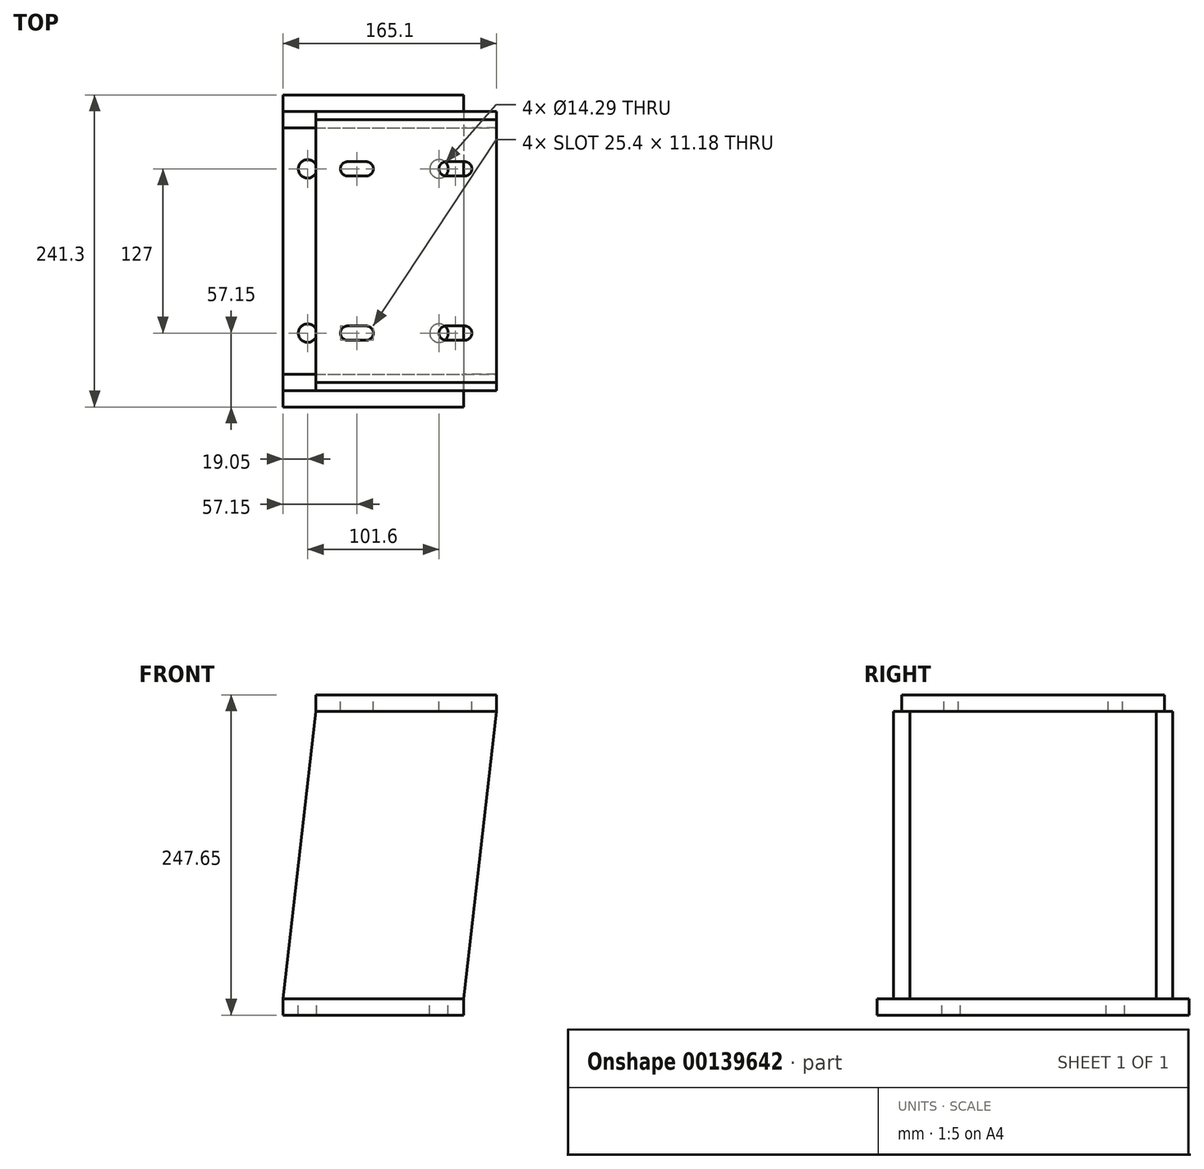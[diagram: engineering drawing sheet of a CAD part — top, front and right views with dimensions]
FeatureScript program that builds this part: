
annotation { "Feature Type Name" : "Feature", "Feature Type Description" : "" }
export const myFeature = defineFeature(function(context is Context, id is Id, definition is map)
    precondition{}
    {
        {
            var Q0;
            Q0=qCreatedBy(makeId("Top.planeOp"),FACE);
            var sketch = newSketch(context, id + "F0", { "sketchPlane" : qUnion([Q0])});
            skLineSegment(sketch, "E0.bottom", {"start": v(-69.85, 120.65) * mm, "end": v(69.85, 120.65) * mm});
            skLineSegment(sketch, "E0.top", {"start": v(-69.85, -120.65) * mm, "end": v(69.85, -120.65) * mm});
            skLineSegment(sketch, "E0.left", {"start": v(-69.85, 120.65) * mm, "end": v(-69.85, -120.65) * mm});
            skLineSegment(sketch, "E0.right", {"start": v(69.85, 120.65) * mm, "end": v(69.85, -120.65) * mm});
            skPoint(sketch, "E0.middle", {"position": v(0, 0) * mm});
            skSolve(sketch);
        }
        {
            var Q0;
            Q0 = qSketchRegion(id + "F0", true);
            extrude(context, id + "F1", {"entities" : qUnion([Q0]), "depth" : 12.7 * mm});
        }
        {
            var Q0;
            Q0=makeQuery(id+"F1.opExtrude","CAP_FACE",FACE,{"disambiguationData":[OSD([sQuery(id+"F0.wireOp",EDGE,"E0.bottom"),sQuery(id+"F0.wireOp",EDGE,"E0.top"),sQuery(id+"F0.wireOp",EDGE,"E0.left"),sQuery(id+"F0.wireOp",EDGE,"E0.right")])],"isStart":false});
            var sketch = newSketch(context, id + "F2", { "sketchPlane" : qUnion([Q0])});
            skLineSegment(sketch, "E1", {"start": v(-129.71, 0) * mm, "end": v(124.43, 0) * mm, "construction": true});
            skLineSegment(sketch, "E2.0", {"start": v(69.85, 120.65) * mm, "end": v(69.85, -120.65) * mm, "construction": true});
            skLineSegment(sketch, "E3.0", {"start": v(50.8, 120.65) * mm, "end": v(50.8, -120.65) * mm, "construction": true});
            skLineSegment(sketch, "E4.0", {"start": v(-50.8, 120.65) * mm, "end": v(-50.8, -120.65) * mm, "construction": true});
            skLineSegment(sketch, "E5.0", {"start": v(-129.71, -63.5) * mm, "end": v(124.43, -63.5) * mm, "construction": true});
            skPoint(sketch, "E6", {"position": v(-50.8, -63.5) * mm});
            skPoint(sketch, "E7", {"position": v(50.8, -63.5) * mm});
            skPoint(sketch, "E8.MirrorP", {"position": v(-50.8, 63.5) * mm});
            skPoint(sketch, "E9.MirrorP", {"position": v(50.8, 63.5) * mm});
            skSolve(sketch);
        }
        {
            var Q0;
            Q0=sQuery(id+"F2.wireOp",VERTEX,"E8.MirrorP");
            var Q1;
            Q1=sQuery(id+"F2.wireOp",VERTEX,"E9.MirrorP");
            var Q2;
            Q2=sQuery(id+"F2.wireOp",VERTEX,"E7");
            var Q3;
            Q3=sQuery(id+"F2.wireOp",VERTEX,"E6");
            var Q4;
            Q4=makeQuery(id+"F1.opExtrude","SWEPT_BODY",BODY,{"disambiguationData":[OSD([sQuery(id+"F0.wireOp",EDGE,"E0.bottom"),sQuery(id+"F0.wireOp",EDGE,"E0.top"),sQuery(id+"F0.wireOp",EDGE,"E0.left"),sQuery(id+"F0.wireOp",EDGE,"E0.right")])]});
            hole(context, id + "F3", {"style" : HoleStyle.SIMPLE, "endStyle" : HoleEndStyle.THROUGH, "holeDiameter" : 14.29 * mm, "locations" : qUnion([Q0, Q1, Q2, Q3]), "scope" : qUnion([Q4]), "isTappedThrough" : true});
        }
        {
            var Q0;
            Q0=makeQuery(id+"F1.opExtrude","CAP_FACE",FACE,{"disambiguationData":[OSD([sQuery(id+"F0.wireOp",EDGE,"E0.bottom"),sQuery(id+"F0.wireOp",EDGE,"E0.top"),sQuery(id+"F0.wireOp",EDGE,"E0.left"),sQuery(id+"F0.wireOp",EDGE,"E0.right")])],"isStart":true});
            cPlane(context, id + "F4", {"entities" : qUnion([Q0]), "cplaneType" : CPlaneType.OFFSET, "offset" : 247.65 * mm, "oppositeDirection" : true, "width" : 152.4 * mm, "height" : 152.4 * mm});
        }
        {
            var Q0;
            Q0=qCreatedBy(id+"F4.planeOp",FACE);
            var sketch = newSketch(context, id + "F5", { "sketchPlane" : qUnion([Q0])});
            skLineSegment(sketch, "E10.0", {"start": v(69.85, -120.65) * mm, "end": v(69.85, 120.65) * mm, "construction": true});
            skLineSegment(sketch, "E11.0", {"start": v(95.25, -101.6) * mm, "end": v(95.25, 101.6) * mm});
            skLineSegment(sketch, "E12.0", {"start": v(-44.45, -101.6) * mm, "end": v(-44.45, 101.6) * mm});
            skLineSegment(sketch, "E13", {"start": v(-120.56, 0) * mm, "end": v(184.47, 0) * mm, "construction": true});
            skPoint(sketch, "E13.endSnap0", {"position": v(-44.45, 0) * mm});
            skLineSegment(sketch, "E14.0", {"start": v(-44.45, -101.6) * mm, "end": v(95.25, -101.6) * mm});
            skLineSegment(sketch, "E15.MirrorCS", {"start": v(-44.45, 101.6) * mm, "end": v(95.25, 101.6) * mm});
            skPoint(sketch, "E16.orphan", {"position": v(-120.56, -101.6) * mm});
            skPoint(sketch, "E17.orphan", {"position": v(-44.45, -120.65) * mm});
            skPoint(sketch, "E18.orphan", {"position": v(184.47, -101.6) * mm});
            skPoint(sketch, "E19.orphan", {"position": v(184.47, 101.6) * mm});
            skPoint(sketch, "E20.orphan", {"position": v(-44.45, 120.65) * mm});
            skPoint(sketch, "E21.orphan", {"position": v(-120.56, 101.6) * mm});
            skLineSegment(sketch, "E22", {"start": v(25.4, -101.6) * mm, "end": v(25.4, 101.6) * mm, "construction": true});
            skLineSegment(sketch, "E23.0", {"start": v(-12.7, -101.6) * mm, "end": v(-12.7, 101.6) * mm, "construction": true});
            skLineSegment(sketch, "E24.0", {"start": v(-5.59, -101.6) * mm, "end": v(-5.59, 101.6) * mm, "construction": true});
            skLineSegment(sketch, "E25.MirrorCS", {"start": v(-19.81, -101.6) * mm, "end": v(-19.81, 101.6) * mm, "construction": true});
            skLineSegment(sketch, "E26", {"start": v(-19.81, -63.5) * mm, "end": v(-5.59, -63.5) * mm});
            skArc(sketch, "E27.0.startCap", {"start": v(-19.81, -69.09) * mm, "mid": v(-25.4, -63.5) * mm, "end": v(-19.81, -57.91) * mm});
            skArc(sketch, "E27.0.endCap", {"start": v(-5.59, -57.91) * mm, "mid": v(0, -63.5) * mm, "end": v(-5.59, -69.09) * mm});
            skLineSegment(sketch, "E27.0.left", {"start": v(-19.81, -57.91) * mm, "end": v(-5.59, -57.91) * mm});
            skLineSegment(sketch, "E27.0.right", {"start": v(-19.81, -69.09) * mm, "end": v(-5.59, -69.09) * mm});
            skArc(sketch, "E28.MirrorCS", {"start": v(56.39, -57.91) * mm, "mid": v(50.8, -63.5) * mm, "end": v(56.39, -69.09) * mm});
            skArc(sketch, "E29.MirrorCS", {"start": v(70.61, -69.09) * mm, "mid": v(76.2, -63.5) * mm, "end": v(70.61, -57.91) * mm});
            skLineSegment(sketch, "E30.MirrorCS", {"start": v(70.61, -69.09) * mm, "end": v(56.39, -69.09) * mm});
            skLineSegment(sketch, "E31.MirrorCS", {"start": v(70.61, -63.5) * mm, "end": v(56.39, -63.5) * mm});
            skLineSegment(sketch, "E32.MirrorCS", {"start": v(70.61, -57.91) * mm, "end": v(56.39, -57.91) * mm});
            skArc(sketch, "E33.MirrorCS", {"start": v(70.61, 69.09) * mm, "mid": v(76.2, 63.5) * mm, "end": v(70.61, 57.91) * mm});
            skLineSegment(sketch, "E34.MirrorCS", {"start": v(70.61, 57.91) * mm, "end": v(56.39, 57.91) * mm});
            skLineSegment(sketch, "E35.MirrorCS", {"start": v(70.61, 69.09) * mm, "end": v(56.39, 69.09) * mm});
            skLineSegment(sketch, "E36.MirrorCS", {"start": v(-19.81, 57.91) * mm, "end": v(-5.59, 57.91) * mm});
            skLineSegment(sketch, "E37.MirrorCS", {"start": v(-19.81, 69.09) * mm, "end": v(-5.59, 69.09) * mm});
            skArc(sketch, "E38.MirrorCS", {"start": v(56.39, 57.91) * mm, "mid": v(50.8, 63.5) * mm, "end": v(56.39, 69.09) * mm});
            skLineSegment(sketch, "E39.MirrorCS", {"start": v(70.61, 63.5) * mm, "end": v(56.39, 63.5) * mm});
            skLineSegment(sketch, "E40.MirrorCS", {"start": v(-19.81, 63.5) * mm, "end": v(-5.59, 63.5) * mm});
            skArc(sketch, "E41.MirrorCS", {"start": v(-19.81, 69.09) * mm, "mid": v(-25.4, 63.5) * mm, "end": v(-19.81, 57.91) * mm});
            skArc(sketch, "E42.MirrorCS", {"start": v(-5.59, 57.91) * mm, "mid": v(0, 63.5) * mm, "end": v(-5.59, 69.09) * mm});
            skSolve(sketch);
        }
        {
            var Q0;
            Q0 = qSketchRegion(id + "F5", true);
            extrude(context, id + "F6", {"entities" : qUnion([Q0]), "depth" : 12.7 * mm});
        }
        {
            var Q0;
            Q0=makeQuery(id+"F6.opExtrude","SWEPT_FACE",FACE,{"disambiguationData":[OSD([sQuery(id+"F5.wireOp",EDGE,"E15.MirrorCS")])]});
            var sketch = newSketch(context, id + "F7", { "sketchPlane" : qUnion([Q0])});
            skLineSegment(sketch, "E43.0", {"start": v(-44.45, 234.95) * mm, "end": v(95.25, 234.95) * mm});
            skLineSegment(sketch, "E44.0", {"start": v(-69.85, 12.7) * mm, "end": v(69.85, 12.7) * mm});
            skLineSegment(sketch, "E45", {"start": v(-69.85, 12.7) * mm, "end": v(-44.45, 234.95) * mm});
            skLineSegment(sketch, "E46", {"start": v(95.25, 234.95) * mm, "end": v(69.85, 12.7) * mm});
            skSolve(sketch);
        }
        {
            var Q0;
            Q0 = qSketchRegion(id + "F7", true);
            extrude(context, id + "F8", {"entities" : qUnion([Q0]), "endBound" : BoundingType.SYMMETRIC, "depth" : 12.7 * mm});
        }
        {
            var Q0;
            Q0=makeQuery(id+"F8.opExtrude","SWEPT_BODY",BODY,{"disambiguationData":[OSD([sQuery(id+"F7.wireOp",EDGE,"E43.0"),sQuery(id+"F7.wireOp",EDGE,"E44.0"),sQuery(id+"F7.wireOp",EDGE,"E45"),sQuery(id+"F7.wireOp",EDGE,"E46")])]});
            var Q1;
            Q1=qCreatedBy(makeId("Front.planeOp"),FACE);
            mirror(context, id + "F9", {"entities" : qUnion([Q0]), "mirrorPlane" : qUnion([Q1])});
        }
    });
